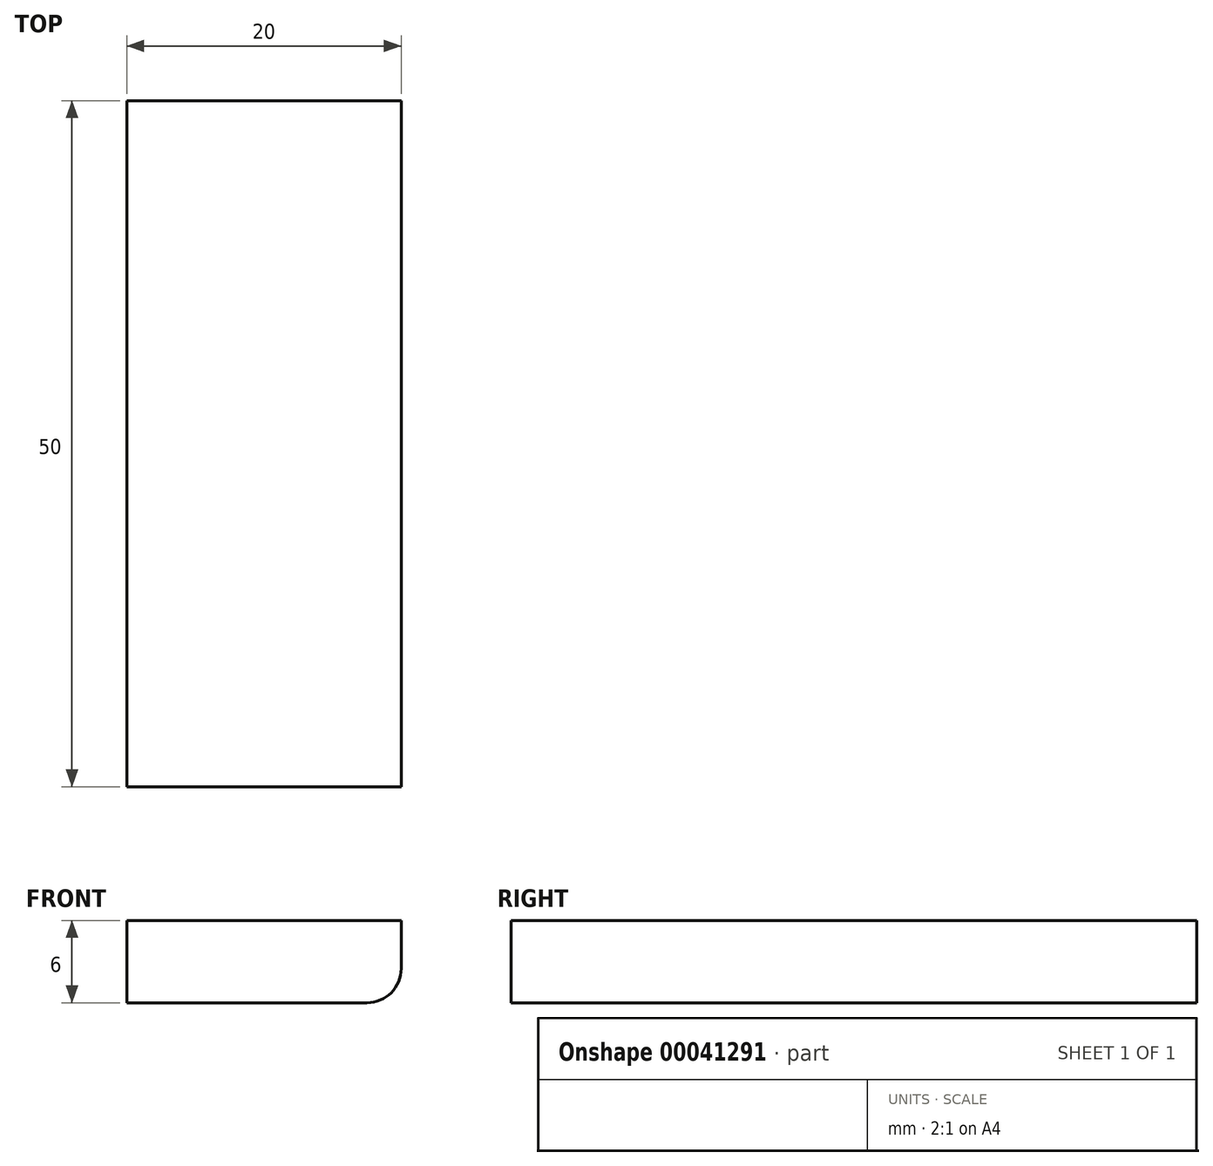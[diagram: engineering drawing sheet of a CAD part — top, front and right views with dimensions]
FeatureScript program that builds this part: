
annotation { "Feature Type Name" : "Feature", "Feature Type Description" : "" }
export const myFeature = defineFeature(function(context is Context, id is Id, definition is map)
    precondition{}
    {
        {
            var Q0;
            Q0=qCreatedBy(makeId("Front.planeOp"),FACE);
            var sketch = newSketch(context, id + "F0", { "sketchPlane" : qUnion([Q0]), "disableImprinting" : false});
            skLineSegment(sketch, "E0", {"start": v(0, 0) * mm, "end": v(0, 26.23) * mm, "construction": true});
            skLineSegment(sketch, "E1", {"start": v(0, 0) * mm, "end": v(36, 0) * mm, "construction": true});
            skLineSegment(sketch, "E2.bottom", {"start": v(36, 0) * mm, "end": v(53.5, 0) * mm});
            skLineSegment(sketch, "E2.top", {"start": v(36, 6) * mm, "end": v(56, 6) * mm});
            skLineSegment(sketch, "E2.left", {"start": v(36, 0) * mm, "end": v(36, 6) * mm});
            skLineSegment(sketch, "E2.right", {"start": v(56, 2.5) * mm, "end": v(56, 6) * mm});
            skPoint(sketch, "E3.visualSharp", {"position": v(56, 0) * mm});
            skArc(sketch, "E3.filletArc", {"start": v(53.5, 0) * mm, "mid": v(55.27, 0.73) * mm, "end": v(56, 2.5) * mm});
            skLineSegment(sketch, "E4.bottom", {"start": v(36, 0) * mm, "end": v(52, 0) * mm});
            skLineSegment(sketch, "E4.top", {"start": v(36, -4) * mm, "end": v(52, -4) * mm});
            skLineSegment(sketch, "E4.left", {"start": v(36, 0) * mm, "end": v(36, -4) * mm});
            skLineSegment(sketch, "E4.right", {"start": v(52, 0) * mm, "end": v(52, -4) * mm});
            skLineSegment(sketch, "E5.bottom", {"start": v(50, -4) * mm, "end": v(36, -4) * mm});
            skLineSegment(sketch, "E5.top", {"start": v(50, -6) * mm, "end": v(36, -6) * mm});
            skLineSegment(sketch, "E5.left", {"start": v(50, -4) * mm, "end": v(50, -6) * mm});
            skLineSegment(sketch, "E5.right", {"start": v(36, -4) * mm, "end": v(36, -6) * mm});
            skLineSegment(sketch, "E6.bottom", {"start": v(46, -6) * mm, "end": v(36, -6) * mm});
            skLineSegment(sketch, "E6.top", {"start": v(46, -12) * mm, "end": v(36, -12) * mm});
            skLineSegment(sketch, "E6.left", {"start": v(46, -6) * mm, "end": v(46, -12) * mm});
            skLineSegment(sketch, "E6.right", {"start": v(36, -6) * mm, "end": v(36, -12) * mm});
            skCircle(sketch, "E7", {"center": v(46, -12) * mm, "radius": 4 * mm});
            skPoint(sketch, "E8", {"position": v(42, -12) * mm});
            skPoint(sketch, "E9", {"position": v(46, -8) * mm});
            skSolve(sketch);
        }
        {
            var Q0;
            Q0=makeQuery(id+"F0.imprint","IMPRINT",FACE,{"disambiguationData":[TD([[makeQuery(id+"F0.imprint","IMPRINT",EDGE,{"derivedFrom":sQuery(id+"F0.wireOp",EDGE,"E2.bottom")}),1.0]])]});
            var Q1;
            {var subQ4=sQuery(id+"F0.wireOp",EDGE,"E2.left");Q1=makeQuery(id+"F0.imprint","IMPRINT",FACE,{"disambiguationData":[TD([[makeQuery(id+"F0.imprint","IMPRINT",EDGE,{"derivedFrom":subQ4}),-1.0]])]});}
            var Q2;
            {var subQ0=sQuery(id+"F0.wireOp",EDGE,"69b44381-6fe6-43a8-8bf0-8cd921e1aed0");var subQ2=sQuery(id+"F0.wireOp",EDGE,"E2.top");var subQ4=makeQuery(id+"F0.imprint","INTERSECT",VERTEX,{"derivedFrom":[subQ2,subQ0]});Q2=makeQuery(id+"F0.imprint","IMPRINT",FACE,{"disambiguationData":[TD([[makeQuery(id+"F0.imprint","IMPRINT",EDGE,{"disambiguationData":[TD([[subQ4,-1.0]])],"derivedFrom":subQ2}),-1.0]])]});}
            var Q3;
            Q3=makeQuery(id+"F0.imprint","IMPRINT",FACE,{"disambiguationData":[TD([[makeQuery(id+"F0.imprint","IMPRINT",EDGE,{"derivedFrom":sQuery(id+"F0.wireOp",EDGE,"E4.bottom")}),-1.0]])]});
            var Q4;
            Q4=makeQuery(id+"F0.imprint","IMPRINT",FACE,{"disambiguationData":[TD([[makeQuery(id+"F0.imprint","IMPRINT",EDGE,{"derivedFrom":sQuery(id+"F0.wireOp",EDGE,"E5.bottom")}),1.0]])]});
            var Q5;
            {var subQ6=sQuery(id+"F0.wireOp",EDGE,"E6.bottom");Q5=makeQuery(id+"F0.imprint","IMPRINT",FACE,{"disambiguationData":[TD([[makeQuery(id+"F0.imprint","IMPRINT",EDGE,{"derivedFrom":subQ6}),1.0]])]});}
            extrude(context, id + "F1", {"entities" : qUnion([Q0, Q1, Q2, Q3, Q4, Q5]), "flatOperationType" : FlatOperationType.REMOVE, "thickness1" : 5 * mm, "thickness2" : 0 * mm, "thickness" : 5 * mm, "depth" : 50 * mm, "offsetDistance" : 25 * mm, "startOffsetBound" : StartOffsetType.BLIND, "startOffsetDistance" : 25 * mm, "symmetric" : true, "domain" : OperationDomain.MODEL});
        }
    });
